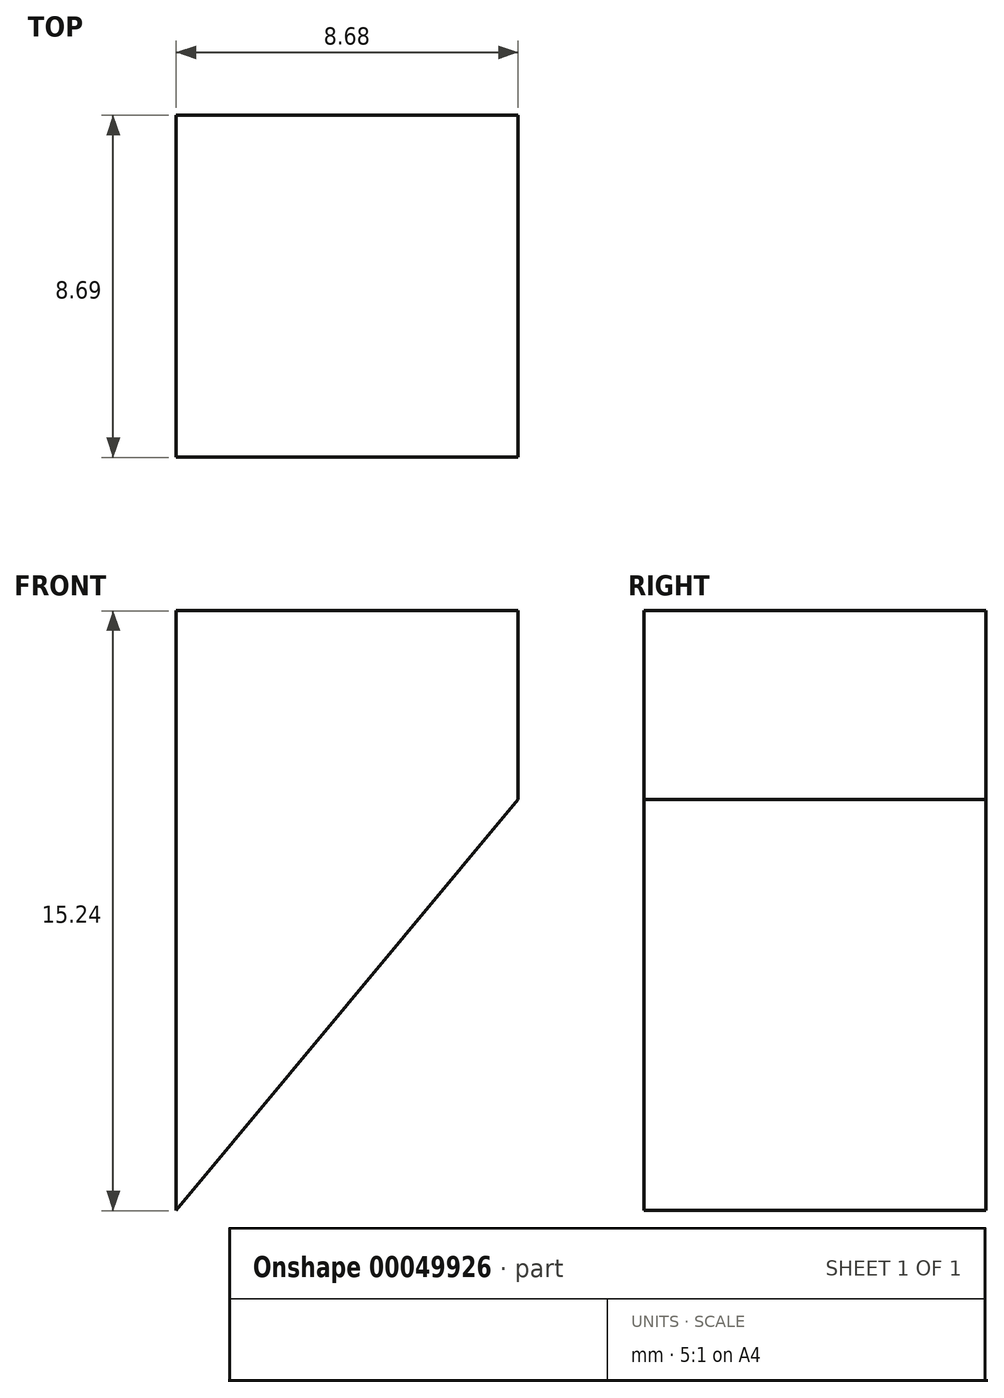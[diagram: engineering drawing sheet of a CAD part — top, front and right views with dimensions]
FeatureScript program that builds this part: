
annotation { "Feature Type Name" : "Feature", "Feature Type Description" : "" }
export const myFeature = defineFeature(function(context is Context, id is Id, definition is map)
    precondition{}
    {
        {
            var Q0;
            Q0=qCreatedBy(makeId("Front.planeOp"),FACE);
            var sketch = newSketch(context, id + "F0", { "sketchPlane" : qUnion([Q0])});
            skLineSegment(sketch, "E0", {"start": v(0.72, 0.54) * mm, "end": v(9.4, 11) * mm});
            skLineSegment(sketch, "E1", {"start": v(0.72, 0.54) * mm, "end": v(0.72, 15.78) * mm});
            skLineSegment(sketch, "E2", {"start": v(0.72, 15.78) * mm, "end": v(9.4, 15.78) * mm});
            skLineSegment(sketch, "E3", {"start": v(9.4, 11) * mm, "end": v(9.4, 15.78) * mm});
            skSolve(sketch);
        }
        {
            var Q0;
            Q0 = qSketchRegion(id + "F0", true);
            extrude(context, id + "F1", {"entities" : qUnion([Q0]), "depth" : 8.7 * mm});
        }
    });
